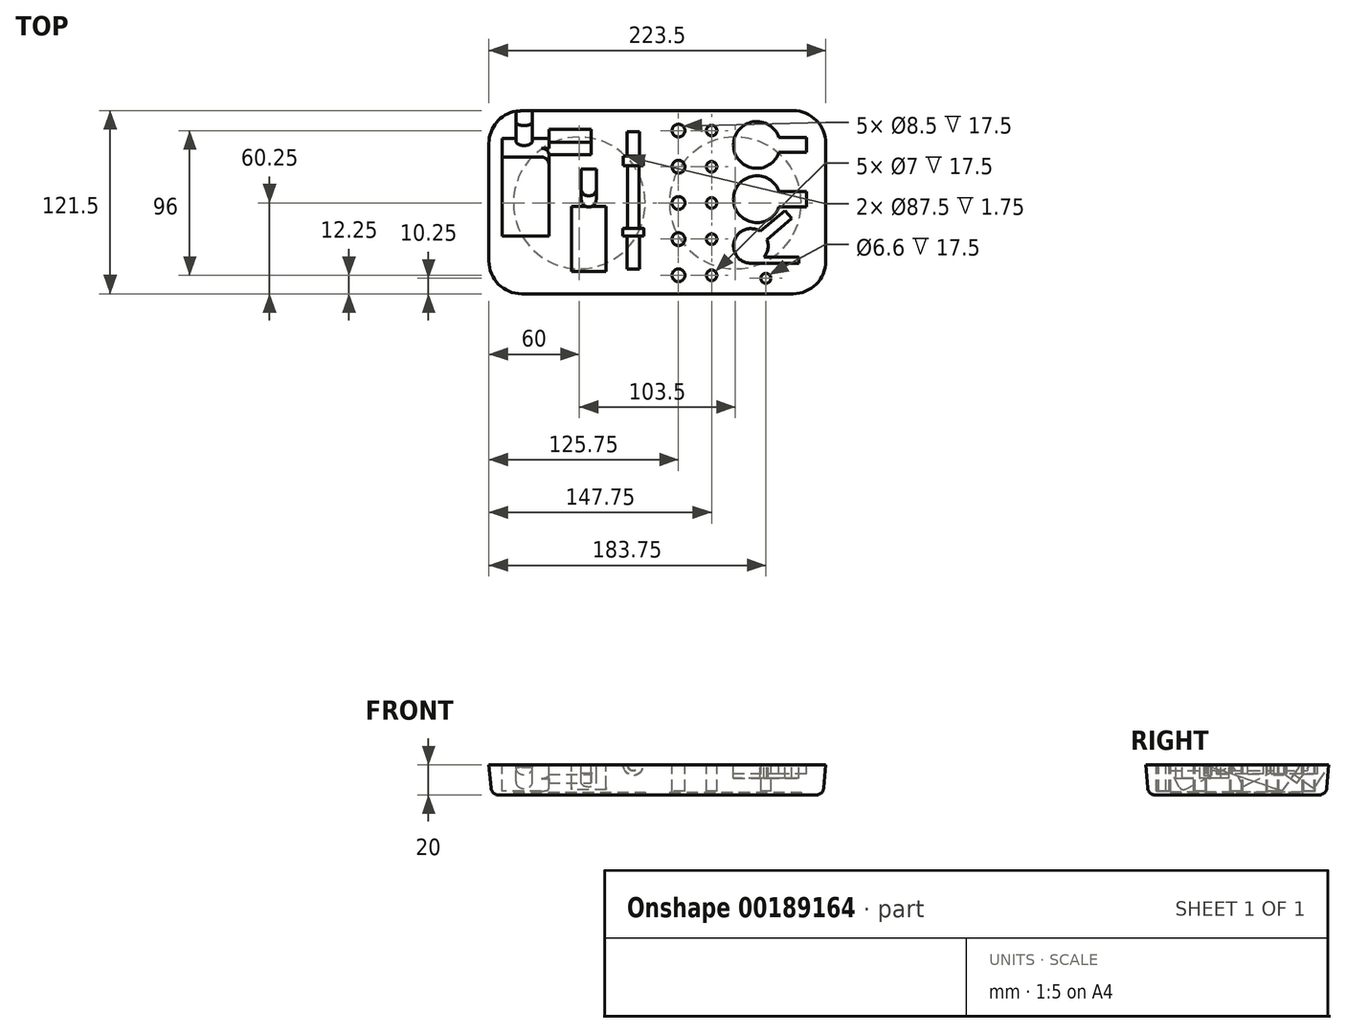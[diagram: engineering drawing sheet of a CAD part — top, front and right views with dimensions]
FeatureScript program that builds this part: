
annotation { "Feature Type Name" : "Feature", "Feature Type Description" : "" }
export const myFeature = defineFeature(function(context is Context, id is Id, definition is map)
    precondition{}
    {
        {
            var Q0;
            Q0=qCreatedBy(makeId("Top.planeOp"),FACE);
            var sketch = newSketch(context, id + "F0", { "sketchPlane" : qUnion([Q0])});
            skLineSegment(sketch, "E0.bottom", {"start": v(20, 0) * mm, "end": v(200, 0) * mm});
            skLineSegment(sketch, "E0.top", {"start": v(20, 118) * mm, "end": v(200, 118) * mm});
            skLineSegment(sketch, "E0.left", {"start": v(0, 20) * mm, "end": v(0, 98) * mm});
            skLineSegment(sketch, "E0.right", {"start": v(220, 20) * mm, "end": v(220, 98) * mm});
            skPoint(sketch, "E1.visualSharp", {"position": v(0, 118) * mm});
            skArc(sketch, "E1.filletArc", {"start": v(20, 118) * mm, "mid": v(5.86, 112.14) * mm, "end": v(0, 98) * mm});
            skPoint(sketch, "E2.visualSharp", {"position": v(220, 118) * mm});
            skArc(sketch, "E2.filletArc", {"start": v(220, 98) * mm, "mid": v(214.14, 112.14) * mm, "end": v(200, 118) * mm});
            skPoint(sketch, "E3.visualSharp", {"position": v(0, 0) * mm});
            skArc(sketch, "E3.filletArc", {"start": v(0, 20) * mm, "mid": v(5.86, 5.86) * mm, "end": v(20, 0) * mm});
            skPoint(sketch, "E4.visualSharp", {"position": v(220, 0) * mm});
            skArc(sketch, "E4.filletArc", {"start": v(200, 0) * mm, "mid": v(214.14, 5.86) * mm, "end": v(220, 20) * mm});
            skSolve(sketch);
        }
        {
            var Q0;
            Q0=makeQuery(id+"F0.imprint","IMPRINT",FACE,{"disambiguationData":[TD([[makeQuery(id+"F0.imprint","IMPRINT",EDGE,{"derivedFrom":sQuery(id+"F0.wireOp",EDGE,"E0.bottom")}),1.0]])]});
            extrude(context, id + "F1", {"entities" : qUnion([Q0]), "depth" : 20 * mm, "hasDraft" : true, "draftAngle" : 5 * degree});
        }
        {
            var Q0;
            Q0=makeQuery(id+"F1.opExtrude","CAP_FACE",FACE,{"disambiguationData":[OSD([sQuery(id+"F0.wireOp",EDGE,"E0.bottom"),sQuery(id+"F0.wireOp",EDGE,"E0.top"),sQuery(id+"F0.wireOp",EDGE,"E0.left"),sQuery(id+"F0.wireOp",EDGE,"E0.right"),sQuery(id+"F0.wireOp",EDGE,"E1.filletArc"),sQuery(id+"F0.wireOp",EDGE,"E2.filletArc"),sQuery(id+"F0.wireOp",EDGE,"E3.filletArc"),sQuery(id+"F0.wireOp",EDGE,"E4.filletArc")])],"isStart":true});
            fillet(context, id + "F2", {"entities" : qUnion([Q0]), "radius" : 5 * mm, "tangentPropagation" : true, "allowEdgeOverflow" : false});
        }
        {
            var Q0;
            Q0=makeQuery(id+"F1.opExtrude","CAP_FACE",FACE,{"disambiguationData":[OSD([sQuery(id+"F0.wireOp",EDGE,"E0.bottom"),sQuery(id+"F0.wireOp",EDGE,"E0.top"),sQuery(id+"F0.wireOp",EDGE,"E0.left"),sQuery(id+"F0.wireOp",EDGE,"E0.right"),sQuery(id+"F0.wireOp",EDGE,"E1.filletArc"),sQuery(id+"F0.wireOp",EDGE,"E2.filletArc"),sQuery(id+"F0.wireOp",EDGE,"E3.filletArc"),sQuery(id+"F0.wireOp",EDGE,"E4.filletArc")])],"isStart":true});
            var sketch = newSketch(context, id + "F3", { "sketchPlane" : qUnion([Q0])});
            skLineSegment(sketch, "E5.bottom", {"start": v(0, 0) * mm, "end": v(58.25, 0) * mm, "construction": true});
            skLineSegment(sketch, "E5.top", {"start": v(0, -58.5) * mm, "end": v(58.25, -58.5) * mm, "construction": true});
            skLineSegment(sketch, "E5.left", {"start": v(0, 0) * mm, "end": v(0, -58.5) * mm, "construction": true});
            skLineSegment(sketch, "E5.right", {"start": v(58.25, 0) * mm, "end": v(58.25, -58.5) * mm, "construction": true});
            skLineSegment(sketch, "E6.bottom", {"start": v(0, 0) * mm, "end": v(161.75, 0) * mm, "construction": true});
            skLineSegment(sketch, "E6.top", {"start": v(0, -58.5) * mm, "end": v(161.75, -58.5) * mm, "construction": true});
            skLineSegment(sketch, "E6.right", {"start": v(161.75, 0) * mm, "end": v(161.75, -58.5) * mm, "construction": true});
            skCircle(sketch, "E7", {"center": v(58.25, -58.5) * mm, "radius": 43.75 * mm});
            skCircle(sketch, "E8", {"center": v(161.75, -58.5) * mm, "radius": 43.75 * mm});
            skSolve(sketch);
        }
        {
            var Q0;
            Q0 = qSketchRegion(id + "F3", true);
            extrude(context, id + "F4", {"entities" : qUnion([Q0]), "operationType" : NewBodyOperationType.REMOVE, "oppositeDirection" : true, "depth" : 1.75 * mm});
        }
        {
            var Q0;
            Q0=qCreatedBy(makeId("Right.planeOp"),FACE);
            cPlane(context, id + "F5", {"entities" : qUnion([Q0]), "cplaneType" : CPlaneType.OFFSET, "offset" : 7 * mm, "width" : 150 * mm, "height" : 150 * mm});
        }
        {
            var Q0;
            Q0=qCreatedBy(id+"F5.planeOp",FACE);
            var sketch = newSketch(context, id + "F6", { "sketchPlane" : qUnion([Q0])});
            skLineSegment(sketch, "E9.bottom", {"start": v(0, 0) * mm, "end": v(89, 0) * mm, "construction": true});
            skLineSegment(sketch, "E9.top", {"start": v(0, 2.5) * mm, "end": v(89, 2.5) * mm, "construction": true});
            skLineSegment(sketch, "E9.left", {"start": v(0, 0) * mm, "end": v(0, 2.5) * mm, "construction": true});
            skLineSegment(sketch, "E9.right", {"start": v(89, 0) * mm, "end": v(89, 2.5) * mm, "construction": true});
            skLineSegment(sketch, "E10", {"start": v(89, 2.5) * mm, "end": v(79, 5.85) * mm});
            skLineSegment(sketch, "E11", {"start": v(89, 2.5) * mm, "end": v(92.31, 7.23) * mm});
            skLineSegment(sketch, "E12", {"start": v(89, 2.5) * mm, "end": v(101.74, 20.69) * mm});
            skLineSegment(sketch, "E13", {"start": v(89, 2.5) * mm, "end": v(32.1, 21.54) * mm});
            skLineSegment(sketch, "E14", {"start": v(101.74, 20.69) * mm, "end": v(32.1, 21.54) * mm});
            skSolve(sketch);
        }
        {
            var Q0;
            Q0 = qSketchRegion(id + "F6", true);
            extrude(context, id + "F7", {"entities" : qUnion([Q0]), "operationType" : NewBodyOperationType.REMOVE, "depth" : 31 * mm});
        }
        {
            var Q0;
            Q0=makeQuery(id+"F7.boolean.opBoolean","COPY",FACE,{"derivedFrom":makeQuery(id+"F7.opExtrude","SWEPT_FACE",FACE,{"disambiguationData":[OSD([sQuery(id+"F6.wireOp",EDGE,"E12")])]})});
            var sketch = newSketch(context, id + "F8", { "sketchPlane" : qUnion([Q0])});
            skLineSegment(sketch, "E15.bottom", {"start": v(7, 53.1) * mm, "end": v(21.6, 53.1) * mm, "construction": true});
            skLineSegment(sketch, "E15.top", {"start": v(7, 71.9) * mm, "end": v(16.1, 71.9) * mm, "construction": true});
            skLineSegment(sketch, "E15.left", {"start": v(7, 53.1) * mm, "end": v(7, 71.9) * mm, "construction": true});
            skLineSegment(sketch, "E15.right", {"start": v(21.6, 53.1) * mm, "end": v(21.6, 71.9) * mm, "construction": true});
            skArc(sketch, "E16", {"start": v(16.1, 71.9) * mm, "mid": v(21.6, 66.4) * mm, "end": v(27.1, 71.9) * mm});
            skLineSegment(sketch, "E17", {"start": v(16.1, 71.9) * mm, "end": v(16.1, 77.85) * mm});
            skLineSegment(sketch, "E18", {"start": v(27.1, 71.9) * mm, "end": v(28.66, 71.9) * mm, "construction": true});
            skLineSegment(sketch, "E19.left", {"start": v(27.1, 71.9) * mm, "end": v(27.1, 77.85) * mm});
            skLineSegment(sketch, "E20", {"start": v(27.1, 77.85) * mm, "end": v(27.1, 104.7) * mm});
            skLineSegment(sketch, "E21", {"start": v(16.1, 77.85) * mm, "end": v(16.1, 104.61) * mm});
            skLineSegment(sketch, "E22", {"start": v(16.1, 104.61) * mm, "end": v(27.1, 104.7) * mm});
            skSolve(sketch);
        }
        {
            var Q0;
            {var subQ0=sQuery(id+"F8.wireOp",EDGE,"E16");var subQ1=makeQuery(id+"F7.boolean.opBoolean","INTERSECT",EDGE,{"derivedFrom":[makeQuery(id+"F1.opExtrude","CAP_FACE",FACE,{"disambiguationData":[OSD([sQuery(id+"F0.wireOp",EDGE,"E0.bottom"),sQuery(id+"F0.wireOp",EDGE,"E0.top"),sQuery(id+"F0.wireOp",EDGE,"E0.left"),sQuery(id+"F0.wireOp",EDGE,"E0.right"),sQuery(id+"F0.wireOp",EDGE,"E1.filletArc"),sQuery(id+"F0.wireOp",EDGE,"E2.filletArc"),sQuery(id+"F0.wireOp",EDGE,"E3.filletArc"),sQuery(id+"F0.wireOp",EDGE,"E4.filletArc")])],"isStart":false}),makeQuery(id+"F7.opExtrude","SWEPT_FACE",FACE,{"disambiguationData":[OSD([sQuery(id+"F6.wireOp",EDGE,"E12")])]})]});var subQ2=makeQuery(id+"F8.imprint","INTERSECT",VERTEX,{"disambiguationData":[OD(0.0)],"derivedFrom":[subQ1,subQ0]});Q0=makeQuery(id+"F8.imprint","IMPRINT",FACE,{"disambiguationData":[TD([[makeQuery(id+"F8.imprint","IMPRINT",EDGE,{"disambiguationData":[TD([[subQ2,-1.0]])],"derivedFrom":subQ0}),1.0]])]});}
            var Q1;
            {var subQ0=sQuery(id+"F8.wireOp",EDGE,"E16");var subQ1=makeQuery(id+"F7.boolean.opBoolean","INTERSECT",EDGE,{"derivedFrom":[makeQuery(id+"F1.opExtrude","CAP_FACE",FACE,{"disambiguationData":[OSD([sQuery(id+"F0.wireOp",EDGE,"E0.bottom"),sQuery(id+"F0.wireOp",EDGE,"E0.top"),sQuery(id+"F0.wireOp",EDGE,"E0.left"),sQuery(id+"F0.wireOp",EDGE,"E0.right"),sQuery(id+"F0.wireOp",EDGE,"E1.filletArc"),sQuery(id+"F0.wireOp",EDGE,"E2.filletArc"),sQuery(id+"F0.wireOp",EDGE,"E3.filletArc"),sQuery(id+"F0.wireOp",EDGE,"E4.filletArc")])],"isStart":false}),makeQuery(id+"F7.opExtrude","SWEPT_FACE",FACE,{"disambiguationData":[OSD([sQuery(id+"F6.wireOp",EDGE,"E12")])]})]});var subQ2=makeQuery(id+"F8.imprint","INTERSECT",VERTEX,{"disambiguationData":[OD(0.0)],"derivedFrom":[subQ1,subQ0]});Q1=makeQuery(id+"F8.imprint","IMPRINT",FACE,{"disambiguationData":[TD([[makeQuery(id+"F8.imprint","IMPRINT",EDGE,{"disambiguationData":[TD([[subQ2,1.0]])],"derivedFrom":subQ0}),1.0]])]});}
            var Q2;
            {var subQ1=sQuery(id+"F8.wireOp",EDGE,"E20");Q2=makeQuery(id+"F8.imprint","IMPRINT",FACE,{"disambiguationData":[TD([[makeQuery(id+"F8.imprint","IMPRINT",EDGE,{"derivedFrom":subQ1}),1.0]])]});}
            var Q3;
            Q3=sQuery(id+"F8.wireOp",EDGE,"E16");
            extrude(context, id + "F9", {"entities" : qUnion([Q0, Q1, Q2]), "operationType" : NewBodyOperationType.REMOVE, "surfaceEntities" : qUnion([Q3]), "oppositeDirection" : true, "depth" : 16 * mm});
        }
        {
            var Q0;
            Q0=makeQuery(id+"F7.boolean.opBoolean","COPY",FACE,{"derivedFrom":makeQuery(id+"F7.opExtrude","SWEPT_FACE",FACE,{"disambiguationData":[OSD([sQuery(id+"F6.wireOp",EDGE,"E12")])]})});
            var sketch = newSketch(context, id + "F10", { "sketchPlane" : qUnion([Q0])});
            skLineSegment(sketch, "E23", {"start": v(38, 53.1) * mm, "end": v(38, 63.1) * mm, "construction": true});
            skLineSegment(sketch, "E24.bottom", {"start": v(38, 63.1) * mm, "end": v(66, 63.1) * mm});
            skLineSegment(sketch, "E24.top", {"start": v(38, 90.3) * mm, "end": v(66, 90.3) * mm});
            skLineSegment(sketch, "E24.left", {"start": v(38, 63.1) * mm, "end": v(38, 90.3) * mm});
            skLineSegment(sketch, "E24.right", {"start": v(66, 63.1) * mm, "end": v(66, 90.3) * mm});
            skSolve(sketch);
        }
        {
            var Q0;
            Q0 = qSketchRegion(id + "F10", true);
            extrude(context, id + "F11", {"entities" : qUnion([Q0]), "operationType" : NewBodyOperationType.REMOVE, "endBound" : BoundingType.SYMMETRIC, "depth" : 10 * mm});
        }
        {
            var Q0;
            Q0=makeQuery(id+"F7.boolean.opBoolean","COPY",FACE,{"derivedFrom":makeQuery(id+"F7.opExtrude","CAP_FACE",FACE,{"disambiguationData":[OSD([sQuery(id+"F6.wireOp",EDGE,"E12"),sQuery(id+"F6.wireOp",EDGE,"E13"),sQuery(id+"F6.wireOp",EDGE,"E14")])],"isStart":false})});
            var sketch = newSketch(context, id + "F12", { "sketchPlane" : qUnion([Q0])});
            skLineSegment(sketch, "E25", {"start": v(-90.64, 13.56) * mm, "end": v(-90.64, 26.05) * mm});
            skLineSegment(sketch, "E26", {"start": v(-90.64, 13.56) * mm, "end": v(-97.23, 22.97) * mm});
            skLineSegment(sketch, "E27", {"start": v(-97.23, 22.97) * mm, "end": v(-90.64, 26.05) * mm});
            skSolve(sketch);
        }
        {
            var Q0;
            {var subQ1=sQuery(id+"F12.wireOp",EDGE,"E25");var subQ4=sQuery(id+"F6.wireOp",EDGE,"E12");var subQ5=makeQuery(id+"F7.opExtrude","CAP_FACE",FACE,{"disambiguationData":[OSD([subQ4,sQuery(id+"F6.wireOp",EDGE,"E13"),sQuery(id+"F6.wireOp",EDGE,"E14")])],"isStart":false});var subQ7=makeQuery(id+"F7.boolean.opBoolean","INTERSECT",EDGE,{"derivedFrom":[makeQuery(id+"F1.opExtrude","CAP_FACE",FACE,{"disambiguationData":[OSD([sQuery(id+"F0.wireOp",EDGE,"E0.bottom"),sQuery(id+"F0.wireOp",EDGE,"E0.top"),sQuery(id+"F0.wireOp",EDGE,"E0.left"),sQuery(id+"F0.wireOp",EDGE,"E0.right"),sQuery(id+"F0.wireOp",EDGE,"E1.filletArc"),sQuery(id+"F0.wireOp",EDGE,"E2.filletArc"),sQuery(id+"F0.wireOp",EDGE,"E3.filletArc"),sQuery(id+"F0.wireOp",EDGE,"E4.filletArc")])],"isStart":false}),subQ5]});var subQ8=makeQuery(id+"F12.imprint","INTERSECT",VERTEX,{"derivedFrom":[subQ7,subQ1]});Q0=makeQuery(id+"F12.imprint","IMPRINT",FACE,{"disambiguationData":[TD([[makeQuery(id+"F12.imprint","IMPRINT",EDGE,{"disambiguationData":[TD([[subQ8,1.0]])],"derivedFrom":subQ1}),1.0]])]});}
            extrude(context, id + "F13", {"entities" : qUnion([Q0]), "operationType" : NewBodyOperationType.REMOVE, "oppositeDirection" : true, "depth" : 28 * mm});
        }
        {
            var Q0;
            {var subQ0=sQuery(id+"F6.wireOp",EDGE,"E12");Q0=makeQuery(id+"F11.boolean.opBoolean","SPLIT",EDGE,{"disambiguationData":[TD([makeQuery(id+"F1.opExtrude","CAP_FACE",FACE,{"disambiguationData":[OSD([sQuery(id+"F0.wireOp",EDGE,"E0.bottom"),sQuery(id+"F0.wireOp",EDGE,"E0.top"),sQuery(id+"F0.wireOp",EDGE,"E0.left"),sQuery(id+"F0.wireOp",EDGE,"E0.right"),sQuery(id+"F0.wireOp",EDGE,"E1.filletArc"),sQuery(id+"F0.wireOp",EDGE,"E2.filletArc"),sQuery(id+"F0.wireOp",EDGE,"E3.filletArc"),sQuery(id+"F0.wireOp",EDGE,"E4.filletArc")])],"isStart":false})])],"derivedFrom":makeQuery(id+"F7.boolean.opBoolean","COPY",EDGE,{"derivedFrom":makeQuery(id+"F7.opExtrude","CAP_EDGE",EDGE,{"disambiguationData":[OSD([subQ0])],"isStart":false})})});}
            var Q1;
            Q1=makeQuery(id+"F13.boolean.opBoolean","COPY",EDGE,{"derivedFrom":makeQuery(id+"F13.opExtrude","CAP_EDGE",EDGE,{"disambiguationData":[OSD([sQuery(id+"F12.wireOp",EDGE,"E25")])],"isStart":true})});
            fillet(context, id + "F14", {"entities" : qUnion([Q0, Q1]), "radius" : 5 * mm, "tangentPropagation" : true, "allowEdgeOverflow" : false});
        }
        {
            var Q0;
            Q0=qCreatedBy(makeId("Right.planeOp"),FACE);
            cPlane(context, id + "F15", {"entities" : qUnion([Q0]), "cplaneType" : CPlaneType.OFFSET, "offset" : 53 * mm, "width" : 150 * mm, "height" : 150 * mm});
        }
        {
            var Q0;
            Q0=qCreatedBy(id+"F15.planeOp",FACE);
            var sketch = newSketch(context, id + "F16", { "sketchPlane" : qUnion([Q0])});
            skLineSegment(sketch, "E28.bottom", {"start": v(0, 0) * mm, "end": v(22, 0) * mm, "construction": true});
            skLineSegment(sketch, "E28.top", {"start": v(0, 2.5) * mm, "end": v(22, 2.5) * mm, "construction": true});
            skLineSegment(sketch, "E28.left", {"start": v(0, 0) * mm, "end": v(0, 2.5) * mm, "construction": true});
            skLineSegment(sketch, "E28.right", {"start": v(22, 0) * mm, "end": v(22, 2.5) * mm, "construction": true});
            skLineSegment(sketch, "E29", {"start": v(22, 2.5) * mm, "end": v(77.56, 2.5) * mm, "construction": true});
            skLineSegment(sketch, "E30", {"start": v(22, 2.5) * mm, "end": v(17.88, 10.58) * mm, "construction": true});
            skLineSegment(sketch, "E31.bottom", {"start": v(22, 2.5) * mm, "end": v(57.64, 20.66) * mm});
            skLineSegment(sketch, "E31.top", {"start": v(8.38, 29.23) * mm, "end": v(44.02, 47.39) * mm});
            skLineSegment(sketch, "E31.left", {"start": v(22, 2.5) * mm, "end": v(8.38, 29.23) * mm});
            skLineSegment(sketch, "E31.right", {"start": v(57.64, 20.66) * mm, "end": v(44.02, 47.39) * mm});
            skSolve(sketch);
        }
        {
            var Q0;
            Q0 = qSketchRegion(id + "F16", true);
            extrude(context, id + "F17", {"entities" : qUnion([Q0]), "operationType" : NewBodyOperationType.REMOVE, "depth" : 23 * mm});
        }
        {
            var Q0;
            Q0=makeQuery(id+"F17.boolean.opBoolean","COPY",FACE,{"derivedFrom":makeQuery(id+"F17.opExtrude","SWEPT_FACE",FACE,{"disambiguationData":[OSD([sQuery(id+"F16.wireOp",EDGE,"E31.bottom")])]})});
            var sketch = newSketch(context, id + "F18", { "sketchPlane" : qUnion([Q0])});
            skLineSegment(sketch, "E32.bottom", {"start": v(53, 20.74) * mm, "end": v(64.5, 20.74) * mm, "construction": true});
            skLineSegment(sketch, "E32.top", {"start": v(53, 63.74) * mm, "end": v(59.5, 63.74) * mm, "construction": true});
            skLineSegment(sketch, "E32.left", {"start": v(53, 20.74) * mm, "end": v(53, 63.74) * mm, "construction": true});
            skLineSegment(sketch, "E32.right", {"start": v(64.5, 20.74) * mm, "end": v(64.5, 63.74) * mm, "construction": true});
            skArc(sketch, "E33", {"start": v(59.5, 63.74) * mm, "mid": v(64.5, 58.74) * mm, "end": v(69.5, 63.74) * mm});
            skLineSegment(sketch, "E34.top", {"start": v(59.5, 78.74) * mm, "end": v(69.5, 78.74) * mm});
            skLineSegment(sketch, "E34.left", {"start": v(59.5, 63.74) * mm, "end": v(59.5, 78.74) * mm});
            skLineSegment(sketch, "E34.right", {"start": v(69.5, 63.74) * mm, "end": v(69.5, 78.74) * mm});
            skSolve(sketch);
        }
        {
            var Q0;
            Q0=makeQuery(id+"F18.imprint","IMPRINT",FACE,{"disambiguationData":[TD([[makeQuery(id+"F18.imprint","IMPRINT",EDGE,{"derivedFrom":sQuery(id+"F18.wireOp",EDGE,"E34.top")}),-1.0]])]});
            var Q1;
            {var subQ0=sQuery(id+"F18.wireOp",EDGE,"E33");var subQ1=makeQuery(id+"F17.boolean.opBoolean","INTERSECT",EDGE,{"derivedFrom":[makeQuery(id+"F1.opExtrude","CAP_FACE",FACE,{"disambiguationData":[OSD([sQuery(id+"F0.wireOp",EDGE,"E0.bottom"),sQuery(id+"F0.wireOp",EDGE,"E0.top"),sQuery(id+"F0.wireOp",EDGE,"E0.left"),sQuery(id+"F0.wireOp",EDGE,"E0.right"),sQuery(id+"F0.wireOp",EDGE,"E1.filletArc"),sQuery(id+"F0.wireOp",EDGE,"E2.filletArc"),sQuery(id+"F0.wireOp",EDGE,"E3.filletArc"),sQuery(id+"F0.wireOp",EDGE,"E4.filletArc")])],"isStart":false}),makeQuery(id+"F17.opExtrude","SWEPT_FACE",FACE,{"disambiguationData":[OSD([sQuery(id+"F16.wireOp",EDGE,"E31.bottom")])]})]});var subQ2=makeQuery(id+"F18.imprint","INTERSECT",VERTEX,{"disambiguationData":[OD(0.0)],"derivedFrom":[subQ1,subQ0]});Q1=makeQuery(id+"F18.imprint","IMPRINT",FACE,{"disambiguationData":[TD([[makeQuery(id+"F18.imprint","IMPRINT",EDGE,{"disambiguationData":[TD([[subQ2,-1.0]])],"derivedFrom":subQ0}),1.0]])]});}
            extrude(context, id + "F19", {"entities" : qUnion([Q0, Q1]), "operationType" : NewBodyOperationType.REMOVE, "oppositeDirection" : true, "depth" : 16 * mm});
        }
        {
            var Q0;
            Q0=makeQuery(id+"F17.boolean.opBoolean","COPY",EDGE,{"derivedFrom":makeQuery(id+"F17.opExtrude","SWEPT_EDGE",EDGE,{"disambiguationData":[OSD([sQuery(id+"F16.wireOp",EDGE,"E31.bottom"),sQuery(id+"F16.wireOp",EDGE,"E31.left")])]})});
            var Q1;
            Q1=makeQuery(id+"F7.boolean.opBoolean","COPY",EDGE,{"derivedFrom":makeQuery(id+"F7.opExtrude","SWEPT_EDGE",EDGE,{"disambiguationData":[OSD([sQuery(id+"F6.wireOp",EDGE,"E12"),sQuery(id+"F6.wireOp",EDGE,"E13")])]})});
            var Q2;
            Q2=makeQuery(id+"F19.boolean.opBoolean","COPY",EDGE,{"derivedFrom":makeQuery(id+"F19.opExtrude","CAP_EDGE",EDGE,{"disambiguationData":[OSD([sQuery(id+"F18.wireOp",EDGE,"E33")])],"isStart":true})});
            var Q3;
            Q3=makeQuery(id+"F9.boolean.opBoolean","COPY",EDGE,{"derivedFrom":makeQuery(id+"F9.opExtrude","CAP_EDGE",EDGE,{"disambiguationData":[OSD([sQuery(id+"F8.wireOp",EDGE,"E16")])],"isStart":true})});
            fillet(context, id + "F20", {"entities" : qUnion([Q0, Q1, Q2, Q3]), "radius" : 3 * mm, "tangentPropagation" : true, "allowEdgeOverflow" : false});
        }
        {
            var Q0;
            Q0=makeQuery(id+"F19.boolean.opBoolean","COPY",FACE,{"derivedFrom":makeQuery(id+"F19.opExtrude","SWEPT_FACE",FACE,{"disambiguationData":[OSD([sQuery(id+"F18.wireOp",EDGE,"E34.right")])]})});
            var sketch = newSketch(context, id + "F21", { "sketchPlane" : qUnion([Q0])});
            skLineSegment(sketch, "E35", {"start": v(-80.94, 14.58) * mm, "end": v(-80.94, 22.64) * mm});
            skLineSegment(sketch, "E36", {"start": v(-80.94, 14.58) * mm, "end": v(-78.18, 20) * mm});
            skLineSegment(sketch, "E37", {"start": v(-78.18, 20) * mm, "end": v(-80.94, 22.64) * mm});
            skSolve(sketch);
        }
        {
            var Q0;
            Q0=makeQuery(id+"F21.imprint","IMPRINT",FACE,{"disambiguationData":[TD([[makeQuery(id+"F21.imprint","IMPRINT",EDGE,{"derivedFrom":sQuery(id+"F21.wireOp",EDGE,"E35")}),-1.0]])]});
            extrude(context, id + "F22", {"entities" : qUnion([Q0]), "operationType" : NewBodyOperationType.REMOVE, "depth" : 10 * mm});
        }
        {
            var Q0;
            Q0=makeQuery(id+"F1.opExtrude","CAP_FACE",FACE,{"disambiguationData":[OSD([sQuery(id+"F0.wireOp",EDGE,"E0.bottom"),sQuery(id+"F0.wireOp",EDGE,"E0.top"),sQuery(id+"F0.wireOp",EDGE,"E0.left"),sQuery(id+"F0.wireOp",EDGE,"E0.right"),sQuery(id+"F0.wireOp",EDGE,"E1.filletArc"),sQuery(id+"F0.wireOp",EDGE,"E2.filletArc"),sQuery(id+"F0.wireOp",EDGE,"E3.filletArc"),sQuery(id+"F0.wireOp",EDGE,"E4.filletArc")])],"isStart":false});
            var sketch = newSketch(context, id + "F23", { "sketchPlane" : qUnion([Q0])});
            skLineSegment(sketch, "E38.bottom", {"start": v(0, 0) * mm, "end": v(94, 0) * mm, "construction": true});
            skLineSegment(sketch, "E38.top", {"start": v(0, 14.5) * mm, "end": v(94, 14.5) * mm, "construction": true});
            skLineSegment(sketch, "E38.left", {"start": v(0, 0) * mm, "end": v(0, 14.5) * mm, "construction": true});
            skLineSegment(sketch, "E38.right", {"start": v(94, 0) * mm, "end": v(94, 14.5) * mm, "construction": true});
            skLineSegment(sketch, "E39.bottom", {"start": v(94, 14.5) * mm, "end": v(98, 14.5) * mm});
            skLineSegment(sketch, "E39.left", {"start": v(94, 14.5) * mm, "end": v(94, 36.7) * mm});
            skLineSegment(sketch, "E39.right", {"start": v(98, 14.5) * mm, "end": v(98, 36.7) * mm});
            skLineSegment(sketch, "E40.bottom", {"start": v(98, 36.7) * mm, "end": v(101, 36.7) * mm});
            skLineSegment(sketch, "E40.top", {"start": v(99.7, 41.7) * mm, "end": v(101, 41.7) * mm});
            skLineSegment(sketch, "E40.left", {"start": v(94, 36.7) * mm, "end": v(94, 41.7) * mm});
            skLineSegment(sketch, "E40.right", {"start": v(101, 36.7) * mm, "end": v(101, 41.7) * mm});
            skLineSegment(sketch, "E41.left", {"start": v(94, 41.7) * mm, "end": v(94, 83.2) * mm});
            skLineSegment(sketch, "E41.right", {"start": v(97.7, 43.7) * mm, "end": v(97.7, 83.2) * mm});
            skLineSegment(sketch, "E42.bottom", {"start": v(97.7, 83.2) * mm, "end": v(100.7, 83.2) * mm});
            skLineSegment(sketch, "E42.top", {"start": v(98, 89.7) * mm, "end": v(100.7, 89.7) * mm});
            skLineSegment(sketch, "E42.left", {"start": v(94, 83.2) * mm, "end": v(94, 89.7) * mm});
            skLineSegment(sketch, "E42.right", {"start": v(100.7, 83.2) * mm, "end": v(100.7, 89.7) * mm});
            skLineSegment(sketch, "E43.top", {"start": v(94, 105.7) * mm, "end": v(98, 105.7) * mm});
            skLineSegment(sketch, "E43.left", {"start": v(94, 89.7) * mm, "end": v(94, 105.7) * mm});
            skLineSegment(sketch, "E43.right", {"start": v(98, 89.7) * mm, "end": v(98, 105.7) * mm});
            skPoint(sketch, "E44.visualSharp", {"position": v(97.7, 41.7) * mm});
            skArc(sketch, "E44.filletArc", {"start": v(97.7, 43.7) * mm, "mid": v(98.29, 42.29) * mm, "end": v(99.7, 41.7) * mm});
            skSolve(sketch);
        }
        {
            var Q0;
            Q0=makeQuery(id+"F23.imprint","IMPRINT",FACE,{"disambiguationData":[TD([[makeQuery(id+"F23.imprint","IMPRINT",EDGE,{"derivedFrom":sQuery(id+"F23.wireOp",EDGE,"E39.bottom")}),1.0]])]});
            var Q1;
            Q1=sQuery(id+"F23.wireOp",EDGE,"E43.left");
            revolve(context, id + "F24", {"operationType" : NewBodyOperationType.REMOVE, "entities" : qUnion([Q0]), "axis" : qUnion([Q1]), "revolveType" : RevolveType.FULL, "oppositeDirection" : true});
        }
        {
            var Q0;
            Q0=makeQuery(id+"F1.opExtrude","CAP_FACE",FACE,{"disambiguationData":[OSD([sQuery(id+"F0.wireOp",EDGE,"E0.bottom"),sQuery(id+"F0.wireOp",EDGE,"E0.top"),sQuery(id+"F0.wireOp",EDGE,"E0.left"),sQuery(id+"F0.wireOp",EDGE,"E0.right"),sQuery(id+"F0.wireOp",EDGE,"E1.filletArc"),sQuery(id+"F0.wireOp",EDGE,"E2.filletArc"),sQuery(id+"F0.wireOp",EDGE,"E3.filletArc"),sQuery(id+"F0.wireOp",EDGE,"E4.filletArc")])],"isStart":false});
            var sketch = newSketch(context, id + "F25", { "sketchPlane" : qUnion([Q0])});
            skLineSegment(sketch, "E45.bottom", {"start": v(0, 0) * mm, "end": v(124, 0) * mm, "construction": true});
            skLineSegment(sketch, "E45.top", {"start": v(0, 10.5) * mm, "end": v(124, 10.5) * mm, "construction": true});
            skLineSegment(sketch, "E45.left", {"start": v(0, 0) * mm, "end": v(0, 10.5) * mm, "construction": true});
            skLineSegment(sketch, "E45.right", {"start": v(124, 0) * mm, "end": v(124, 10.5) * mm, "construction": true});
            skLineSegment(sketch, "E46.bottom", {"start": v(124, 10.5) * mm, "end": v(146, 10.5) * mm, "construction": true});
            skLineSegment(sketch, "E46.top", {"start": v(124, 34.5) * mm, "end": v(146, 34.5) * mm, "construction": true});
            skLineSegment(sketch, "E46.left", {"start": v(124, 10.5) * mm, "end": v(124, 34.5) * mm, "construction": true});
            skLineSegment(sketch, "E46.right", {"start": v(146, 10.5) * mm, "end": v(146, 34.5) * mm, "construction": true});
            skLineSegment(sketch, "E47.top", {"start": v(124, 58.5) * mm, "end": v(146, 58.5) * mm, "construction": true});
            skLineSegment(sketch, "E47.left", {"start": v(124, 34.5) * mm, "end": v(124, 58.5) * mm, "construction": true});
            skLineSegment(sketch, "E47.right", {"start": v(146, 34.5) * mm, "end": v(146, 58.5) * mm, "construction": true});
            skLineSegment(sketch, "E48.top", {"start": v(124, 82.5) * mm, "end": v(146, 82.5) * mm, "construction": true});
            skLineSegment(sketch, "E48.left", {"start": v(124, 58.5) * mm, "end": v(124, 82.5) * mm, "construction": true});
            skLineSegment(sketch, "E48.right", {"start": v(146, 58.5) * mm, "end": v(146, 82.5) * mm, "construction": true});
            skLineSegment(sketch, "E49.top", {"start": v(124, 106.5) * mm, "end": v(146, 106.5) * mm, "construction": true});
            skLineSegment(sketch, "E49.left", {"start": v(124, 82.5) * mm, "end": v(124, 106.5) * mm, "construction": true});
            skLineSegment(sketch, "E49.right", {"start": v(146, 82.5) * mm, "end": v(146, 106.5) * mm, "construction": true});
            skCircle(sketch, "E50", {"center": v(124, 106.5) * mm, "radius": 4.25 * mm});
            skCircle(sketch, "E51", {"center": v(124, 82.5) * mm, "radius": 4.25 * mm});
            skCircle(sketch, "E52", {"center": v(124, 58.5) * mm, "radius": 4.25 * mm});
            skCircle(sketch, "E53", {"center": v(124, 34.5) * mm, "radius": 4.25 * mm});
            skCircle(sketch, "E54", {"center": v(124, 10.5) * mm, "radius": 4.25 * mm});
            skCircle(sketch, "E55", {"center": v(146, 10.5) * mm, "radius": 3.5 * mm});
            skCircle(sketch, "E56", {"center": v(146, 34.5) * mm, "radius": 3.5 * mm});
            skCircle(sketch, "E57", {"center": v(146, 58.5) * mm, "radius": 3.5 * mm});
            skCircle(sketch, "E58", {"center": v(146, 82.5) * mm, "radius": 3.5 * mm});
            skCircle(sketch, "E59", {"center": v(146, 106.5) * mm, "radius": 3.5 * mm});
            skLineSegment(sketch, "E60.bottom", {"start": v(146, 10.5) * mm, "end": v(182, 10.5) * mm, "construction": true});
            skLineSegment(sketch, "E60.top", {"start": v(146, 8.5) * mm, "end": v(182, 8.5) * mm, "construction": true});
            skLineSegment(sketch, "E60.left", {"start": v(146, 10.5) * mm, "end": v(146, 8.5) * mm, "construction": true});
            skLineSegment(sketch, "E60.right", {"start": v(182, 10.5) * mm, "end": v(182, 8.5) * mm, "construction": true});
            skCircle(sketch, "E61", {"center": v(182, 8.5) * mm, "radius": 3.3 * mm});
            skSolve(sketch);
        }
        {
            var Q0;
            Q0 = qSketchRegion(id + "F25", true);
            extrude(context, id + "F26", {"entities" : qUnion([Q0]), "operationType" : NewBodyOperationType.REMOVE, "oppositeDirection" : true, "depth" : 17.5 * mm});
        }
        {
            var Q0;
            Q0=makeQuery(id+"F1.opExtrude","CAP_FACE",FACE,{"disambiguationData":[OSD([sQuery(id+"F0.wireOp",EDGE,"E0.bottom"),sQuery(id+"F0.wireOp",EDGE,"E0.top"),sQuery(id+"F0.wireOp",EDGE,"E0.left"),sQuery(id+"F0.wireOp",EDGE,"E0.right"),sQuery(id+"F0.wireOp",EDGE,"E1.filletArc"),sQuery(id+"F0.wireOp",EDGE,"E2.filletArc"),sQuery(id+"F0.wireOp",EDGE,"E3.filletArc"),sQuery(id+"F0.wireOp",EDGE,"E4.filletArc")])],"isStart":false});
            var sketch = newSketch(context, id + "F27", { "sketchPlane" : qUnion([Q0])});
            skLineSegment(sketch, "E62.bottom", {"start": v(0, 0) * mm, "end": v(172, 0) * mm, "construction": true});
            skLineSegment(sketch, "E62.top", {"start": v(0, 30) * mm, "end": v(172, 30) * mm, "construction": true});
            skLineSegment(sketch, "E62.left", {"start": v(0, 0) * mm, "end": v(0, 30) * mm, "construction": true});
            skLineSegment(sketch, "E62.right", {"start": v(172, 0) * mm, "end": v(172, 30) * mm, "construction": true});
            skArc(sketch, "E63", {"start": v(180.72, 22.5) * mm, "mid": v(183.33, 28.02) * mm, "end": v(182.75, 34.1) * mm});
            skLineSegment(sketch, "E64", {"start": v(172, 18.5) * mm, "end": v(204, 18.5) * mm});
            skLineSegment(sketch, "E65", {"start": v(204, 18.5) * mm, "end": v(204, 22.5) * mm});
            skLineSegment(sketch, "E66", {"start": v(204, 22.5) * mm, "end": v(180.72, 22.5) * mm});
            skLineSegment(sketch, "E67.bottom", {"start": v(204, 18.5) * mm, "end": v(196, 18.5) * mm, "construction": true});
            skLineSegment(sketch, "E67.top", {"start": v(204, 52) * mm, "end": v(196, 52) * mm, "construction": true});
            skLineSegment(sketch, "E67.left", {"start": v(204, 18.5) * mm, "end": v(204, 52) * mm, "construction": true});
            skLineSegment(sketch, "E67.right", {"start": v(196, 18.5) * mm, "end": v(196, 52) * mm, "construction": true});
            skLineSegment(sketch, "E68", {"start": v(196, 52) * mm, "end": v(194.7, 53.52) * mm});
            skLineSegment(sketch, "E69", {"start": v(196, 52) * mm, "end": v(199.25, 48.2) * mm});
            skLineSegment(sketch, "E70", {"start": v(194.7, 53.52) * mm, "end": v(178.02, 39.8) * mm});
            skLineSegment(sketch, "E71", {"start": v(199.25, 48.2) * mm, "end": v(182.75, 34.1) * mm});
            skArc(sketch, "E72.trimOffspring", {"start": v(178.02, 39.8) * mm, "mid": v(160.93, 33.13) * mm, "end": v(172, 18.5) * mm});
            skLineSegment(sketch, "E73.bottom", {"start": v(172, 30) * mm, "end": v(176, 30) * mm, "construction": true});
            skLineSegment(sketch, "E73.top", {"start": v(172, 61) * mm, "end": v(176, 61) * mm, "construction": true});
            skLineSegment(sketch, "E73.left", {"start": v(172, 30) * mm, "end": v(172, 61) * mm, "construction": true});
            skLineSegment(sketch, "E73.right", {"start": v(176, 30) * mm, "end": v(176, 61) * mm, "construction": true});
            skLineSegment(sketch, "E74", {"start": v(176, 61) * mm, "end": v(176, 97) * mm, "construction": true});
            skArc(sketch, "E75", {"start": v(190.67, 102) * mm, "mid": v(160.5, 97) * mm, "end": v(190.67, 92) * mm});
            skLineSegment(sketch, "E76.top", {"start": v(190.67, 102) * mm, "end": v(209, 102) * mm});
            skLineSegment(sketch, "E76.right", {"start": v(209, 97) * mm, "end": v(209, 102) * mm});
            skLineSegment(sketch, "E77", {"start": v(209, 97) * mm, "end": v(209, 92) * mm});
            skLineSegment(sketch, "E78", {"start": v(209, 92) * mm, "end": v(190.67, 92) * mm});
            skLineSegment(sketch, "E79", {"start": v(176, 79) * mm, "end": v(191.23, 79) * mm, "construction": true});
            skLineSegment(sketch, "E80.MirrorCS", {"start": v(209, 66) * mm, "end": v(190.67, 66) * mm});
            skLineSegment(sketch, "E81.MirrorCS", {"start": v(209, 61) * mm, "end": v(209, 66) * mm});
            skLineSegment(sketch, "E82.MirrorCS", {"start": v(190.67, 56) * mm, "end": v(209, 56) * mm});
            skLineSegment(sketch, "E83.MirrorCS", {"start": v(209, 61) * mm, "end": v(209, 56) * mm});
            skArc(sketch, "E84.MirrorCS", {"start": v(190.67, 56) * mm, "mid": v(160.5, 61) * mm, "end": v(190.67, 66) * mm});
            skSolve(sketch);
        }
        {
            var Q0;
            Q0=makeQuery(id+"F27.imprint","IMPRINT",FACE,{"disambiguationData":[TD([[makeQuery(id+"F27.imprint","IMPRINT",EDGE,{"derivedFrom":sQuery(id+"F27.wireOp",EDGE,"E75")}),1.0]])]});
            var Q1;
            Q1=makeQuery(id+"F27.imprint","IMPRINT",FACE,{"disambiguationData":[TD([[makeQuery(id+"F27.imprint","IMPRINT",EDGE,{"derivedFrom":sQuery(id+"F27.wireOp",EDGE,"E80.MirrorCS")}),1.0]])]});
            var Q2;
            Q2=makeQuery(id+"F27.imprint","IMPRINT",FACE,{"disambiguationData":[TD([[makeQuery(id+"F27.imprint","IMPRINT",EDGE,{"derivedFrom":sQuery(id+"F27.wireOp",EDGE,"E63")}),1.0]])]});
            extrude(context, id + "F28", {"entities" : qUnion([Q0, Q1, Q2]), "operationType" : NewBodyOperationType.REMOVE, "oppositeDirection" : true, "depth" : 6 * mm});
        }
        {
            var Q0;
            Q0=makeQuery(id+"F28.boolean.opBoolean","COPY",FACE,{"derivedFrom":makeQuery(id+"F28.opExtrude","CAP_FACE",FACE,{"disambiguationData":[OSD([sQuery(id+"F27.wireOp",EDGE,"E63"),sQuery(id+"F27.wireOp",EDGE,"E64"),sQuery(id+"F27.wireOp",EDGE,"E65"),sQuery(id+"F27.wireOp",EDGE,"E66"),sQuery(id+"F27.wireOp",EDGE,"E68"),sQuery(id+"F27.wireOp",EDGE,"E69"),sQuery(id+"F27.wireOp",EDGE,"E70"),sQuery(id+"F27.wireOp",EDGE,"E71"),sQuery(id+"F27.wireOp",EDGE,"E72.trimOffspring")])],"isStart":false})});
            extrude(context, id + "F29", {"entities" : qUnion([Q0]), "operationType" : NewBodyOperationType.REMOVE, "oppositeDirection" : true, "depth" : 3 * mm});
        }
    });
